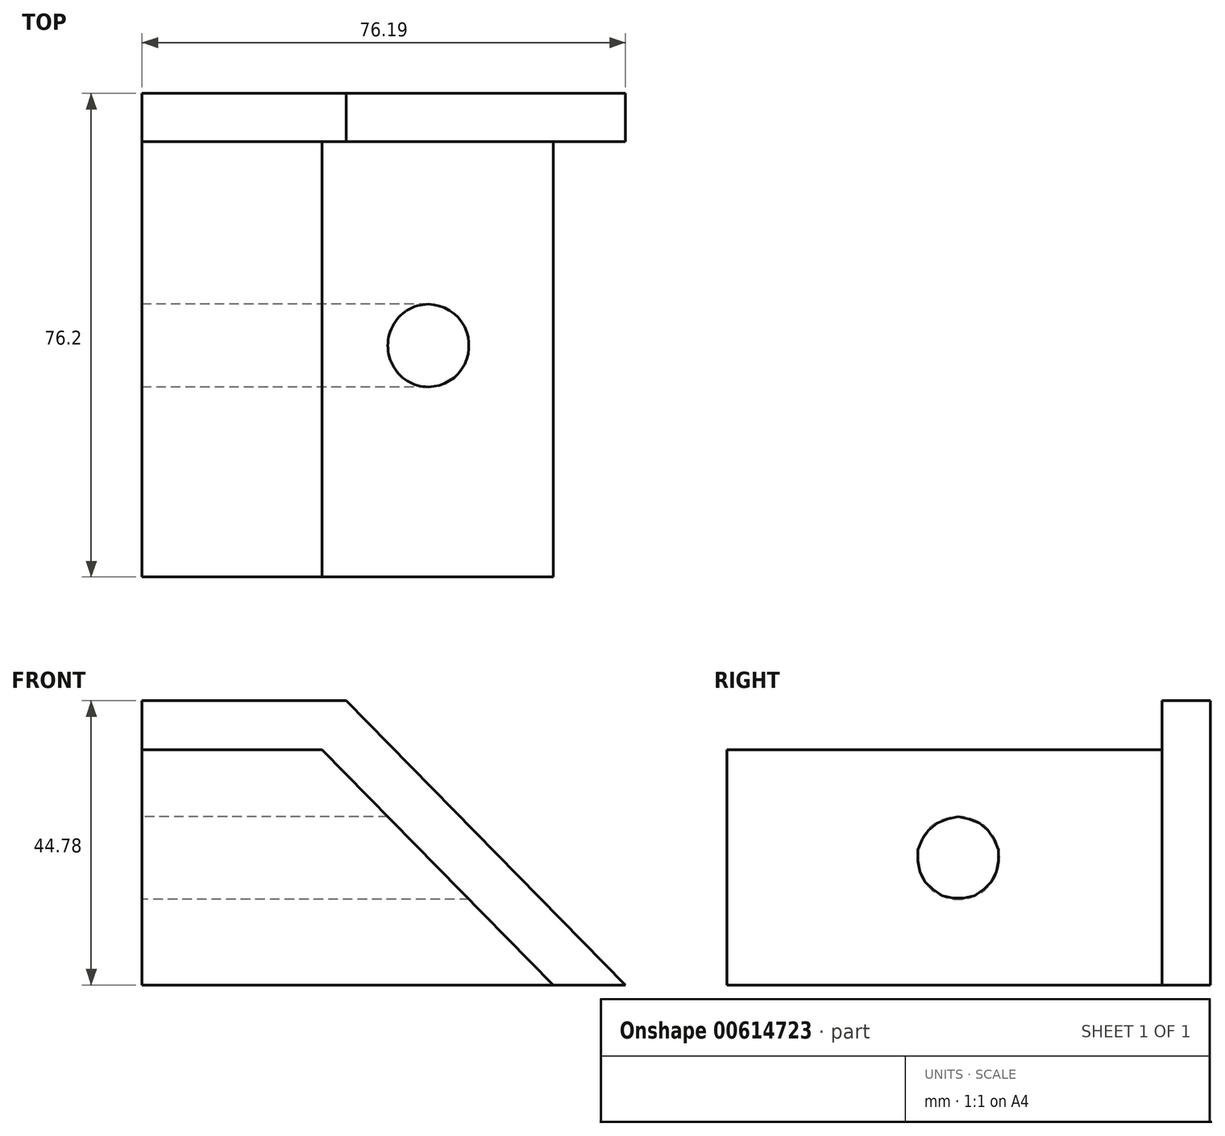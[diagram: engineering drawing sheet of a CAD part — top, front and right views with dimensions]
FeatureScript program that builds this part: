
annotation { "Feature Type Name" : "Feature", "Feature Type Description" : "" }
export const myFeature = defineFeature(function(context is Context, id is Id, definition is map)
    precondition{}
    {
        {
            var Q0;
            Q0=qCreatedBy(makeId("Front.planeOp"),FACE);
            var sketch = newSketch(context, id + "F0", { "sketchPlane" : qUnion([Q0])});
            skLineSegment(sketch, "E0", {"start": v(0, 0) * mm, "end": v(0, 44.78) * mm});
            skLineSegment(sketch, "E1", {"start": v(0, 44.78) * mm, "end": v(32.16, 44.78) * mm});
            skLineSegment(sketch, "E2", {"start": v(32.16, 44.78) * mm, "end": v(76.19, 0) * mm});
            skLineSegment(sketch, "E3", {"start": v(76.19, 0) * mm, "end": v(0, 0) * mm});
            skLineSegment(sketch, "E4", {"start": v(0, 37.08) * mm, "end": v(28.36, 37.08) * mm});
            skLineSegment(sketch, "E5", {"start": v(28.36, 37.08) * mm, "end": v(64.8, 0) * mm});
            skSolve(sketch);
        }
        {
            var Q0;
            {var subQ3=sQuery(id+"F0.wireOp",EDGE,"E4");Q0=makeQuery(id+"F0.imprint","IMPRINT",FACE,{"disambiguationData":[TD([[makeQuery(id+"F0.imprint","IMPRINT",EDGE,{"derivedFrom":subQ3}),-1.0]])]});}
            extrude(context, id + "F1", {"entities" : qUnion([Q0]), "depth" : 76.2 * mm, "offsetDistance" : 25.4 * mm});
        }
        {
            var Q0;
            {var subQ3=sQuery(id+"F0.wireOp",EDGE,"E1");Q0=makeQuery(id+"F0.imprint","IMPRINT",FACE,{"disambiguationData":[TD([[makeQuery(id+"F0.imprint","IMPRINT",EDGE,{"derivedFrom":subQ3}),-1.0]])]});}
            extrude(context, id + "F2", {"entities" : qUnion([Q0]), "operationType" : NewBodyOperationType.ADD, "depth" : 7.62 * mm, "offsetDistance" : 25.4 * mm});
        }
        {
            var Q0;
            {var subQ0=sQuery(id+"F0.wireOp",EDGE,"E0");Q0=makeQuery(id+"F2.boolean.opBoolean","MERGE",FACE,{"derivedFrom":[makeQuery(id+"F1.opExtrude","SWEPT_FACE",FACE,{"disambiguationData":[OSD([subQ0])]}),makeQuery(id+"F2.opExtrude","SWEPT_FACE",FACE,{"disambiguationData":[OSD([subQ0])]})]});}
            var sketch = newSketch(context, id + "F3", { "sketchPlane" : qUnion([Q0])});
            skCircle(sketch, "E6", {"center": v(39.74, 20) * mm, "radius": 6.52 * mm});
            skSolve(sketch);
        }
        {
            var Q0;
            Q0 = qSketchRegion(id + "F3", true);
            extrude(context, id + "F4", {"entities" : qUnion([Q0]), "operationType" : NewBodyOperationType.REMOVE, "oppositeDirection" : true, "depth" : 101.6 * mm, "offsetDistance" : 25.4 * mm});
        }
    });
